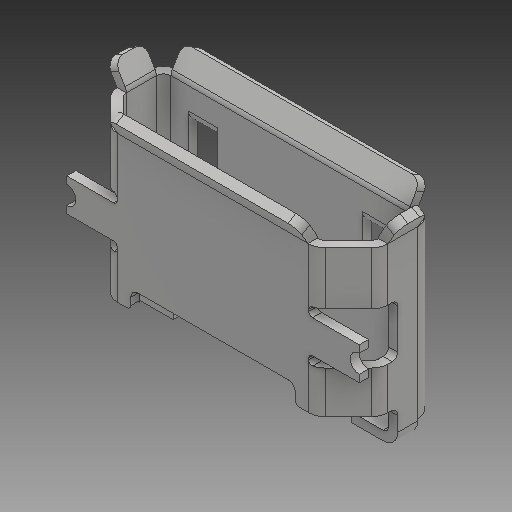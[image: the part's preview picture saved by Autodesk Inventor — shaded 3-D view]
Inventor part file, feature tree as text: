
AUTODESK INVENTOR PART (.ipt)
format: ipt  version: 2018 (Build 220112000, 112)  size: 267,776 bytes
history: native  units: mm
features: mirror x1
ambient origin geometry x8: Origin, YZ Plane, XZ Plane, XY Plane, X Axis, Y Axis, Z Axis, Center Point
bodies: Volumenkörper1 (feature_tree)
feature tree (1):
  mirror  "Mirror2"
